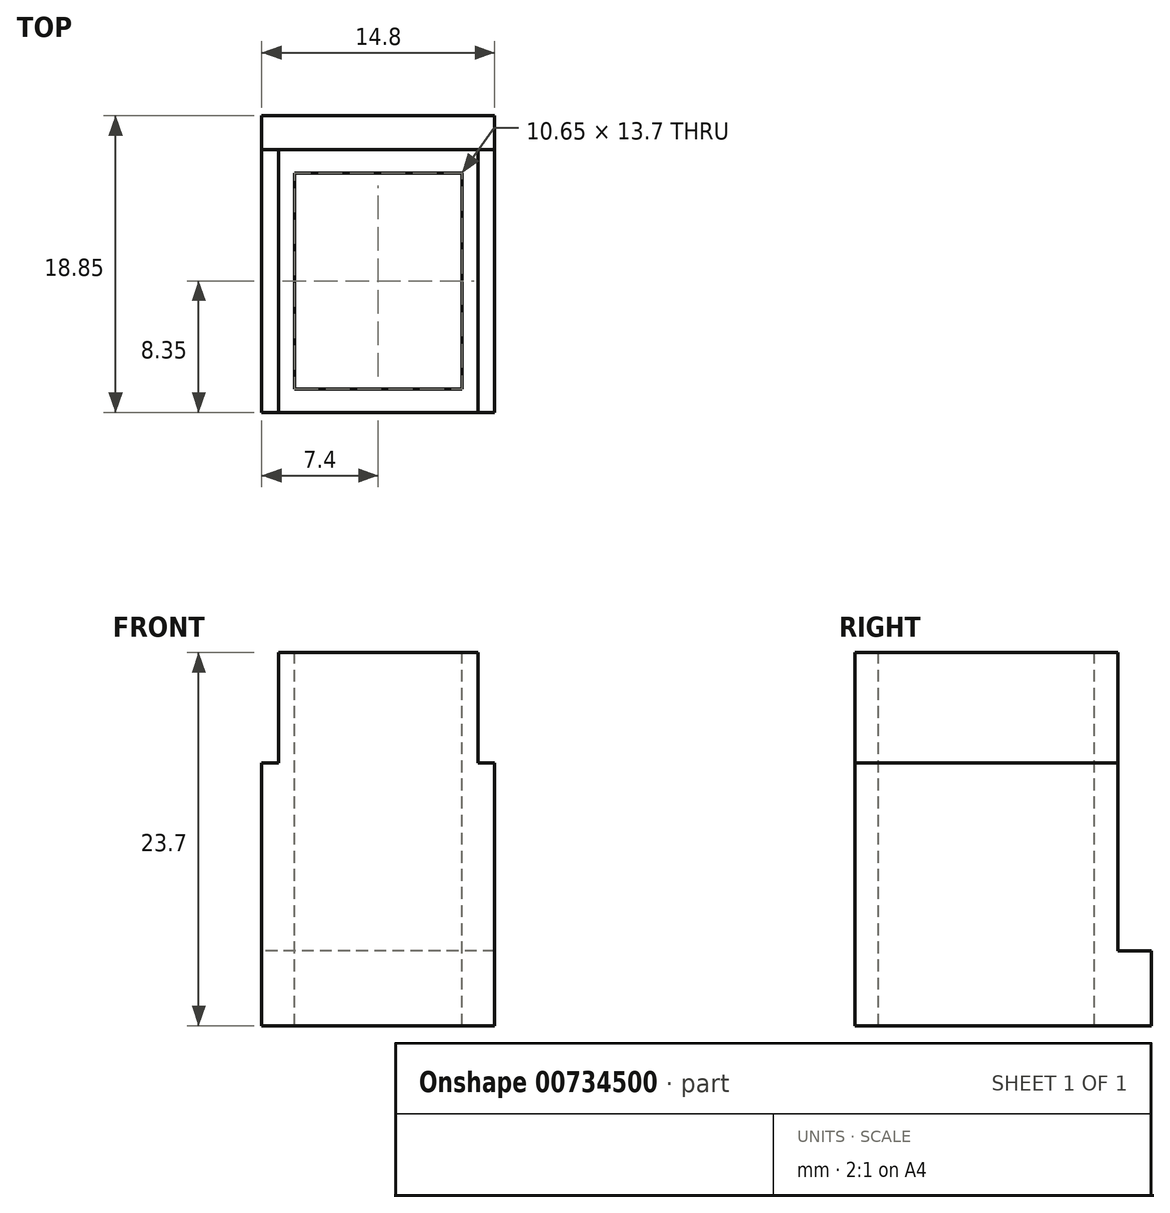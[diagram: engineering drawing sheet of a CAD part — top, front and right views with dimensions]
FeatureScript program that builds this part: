
annotation { "Feature Type Name" : "Feature", "Feature Type Description" : "" }
export const myFeature = defineFeature(function(context is Context, id is Id, definition is map)
    precondition{}
    {
        {
            var Q0;
            Q0=qCreatedBy(makeId("Top.planeOp"),FACE);
            var sketch = newSketch(context, id + "F0", { "sketchPlane" : qUnion([Q0])});
            skLineSegment(sketch, "E0.bottom", {"start": v(5.9, 6.85) * mm, "end": v(-5.9, 6.85) * mm});
            skLineSegment(sketch, "E0.top", {"start": v(5.9, -6.85) * mm, "end": v(-5.9, -6.85) * mm});
            skLineSegment(sketch, "E0.left", {"start": v(5.9, 6.85) * mm, "end": v(5.9, -6.85) * mm});
            skLineSegment(sketch, "E0.right", {"start": v(-5.9, 6.85) * mm, "end": v(-5.9, -6.85) * mm});
            skPoint(sketch, "E0.middle", {"position": v(0, 0) * mm});
            skLineSegment(sketch, "E1.0", {"start": v(-7.4, 8.35) * mm, "end": v(-7.4, -8.35) * mm});
            skLineSegment(sketch, "E1.1", {"start": v(7.4, 8.35) * mm, "end": v(-7.4, 8.35) * mm});
            skLineSegment(sketch, "E1.2", {"start": v(7.4, 8.35) * mm, "end": v(7.4, -8.35) * mm});
            skLineSegment(sketch, "E1.3", {"start": v(7.4, -8.35) * mm, "end": v(-7.4, -8.35) * mm});
            skSolve(sketch);
        }
        {
            var Q0;
            Q0 = qSketchRegion(id + "F0", true);
            extrude(context, id + "F1", {"entities" : qUnion([Q0]), "depth" : 11.95 * mm, "offsetDistance" : 25.4 * mm});
        }
        {
            var Q0;
            Q0=makeQuery(id+"F1.opExtrude","CAP_FACE",FACE,{"disambiguationData":[OSD([sQuery(id+"F0.wireOp",EDGE,"E0.bottom"),sQuery(id+"F0.wireOp",EDGE,"E0.top"),sQuery(id+"F0.wireOp",EDGE,"E0.left"),sQuery(id+"F0.wireOp",EDGE,"E0.right"),sQuery(id+"F0.wireOp",EDGE,"E1.0"),sQuery(id+"F0.wireOp",EDGE,"E1.1"),sQuery(id+"F0.wireOp",EDGE,"E1.2"),sQuery(id+"F0.wireOp",EDGE,"E1.3")])],"isStart":false});
            var sketch = newSketch(context, id + "F2", { "sketchPlane" : qUnion([Q0])});
            skLineSegment(sketch, "E2.bottom", {"start": v(6.32, 8.35) * mm, "end": v(-6.33, 8.35) * mm});
            skLineSegment(sketch, "E2.top", {"start": v(6.33, -8.35) * mm, "end": v(-6.32, -8.35) * mm});
            skLineSegment(sketch, "E2.left", {"start": v(6.32, 8.35) * mm, "end": v(6.33, -8.35) * mm});
            skLineSegment(sketch, "E2.right", {"start": v(-6.33, 8.35) * mm, "end": v(-6.33, -8.35) * mm});
            skPoint(sketch, "E2.middle", {"position": v(0, 0) * mm});
            skLineSegment(sketch, "E3.0", {"start": v(-5.33, 7.35) * mm, "end": v(-5.33, -7.35) * mm});
            skLineSegment(sketch, "E3.1", {"start": v(5.32, 7.35) * mm, "end": v(-5.33, 7.35) * mm});
            skLineSegment(sketch, "E3.2", {"start": v(5.32, 7.35) * mm, "end": v(5.33, -7.35) * mm});
            skLineSegment(sketch, "E3.3", {"start": v(5.33, -7.35) * mm, "end": v(-5.33, -7.35) * mm});
            skSolve(sketch);
        }
        {
            var Q0;
            Q0 = qSketchRegion(id + "F2", true);
            extrude(context, id + "F3", {"entities" : qUnion([Q0]), "operationType" : NewBodyOperationType.ADD, "depth" : 7 * mm, "offsetDistance" : 25.4 * mm});
        }
        {
            var Q0;
            {var subQ1=sQuery(id+"F0.wireOp",EDGE,"E0.right");var subQ3=sQuery(id+"F2.wireOp",EDGE,"E3.0");Q0=makeQuery(id+"F3.boolean.opBoolean","SPLIT",FACE,{"disambiguationData":[TD([makeQuery(id+"F1.opExtrude","SWEPT_FACE",FACE,{"disambiguationData":[OSD([subQ1])]})])],"derivedFrom":makeQuery(id+"F3.opExtrude","CAP_FACE",FACE,{"disambiguationData":[OSD([sQuery(id+"F2.wireOp",EDGE,"E2.bottom"),sQuery(id+"F2.wireOp",EDGE,"E2.top"),sQuery(id+"F2.wireOp",EDGE,"E2.left"),sQuery(id+"F2.wireOp",EDGE,"E2.right"),subQ3,sQuery(id+"F2.wireOp",EDGE,"E3.1"),sQuery(id+"F2.wireOp",EDGE,"E3.2"),sQuery(id+"F2.wireOp",EDGE,"E3.3")])],"isStart":true})});}
            var sketch = newSketch(context, id + "F4", { "sketchPlane" : qUnion([Q0])});
            skLineSegment(sketch, "E4.bottom", {"start": v(-5.9, 6.85) * mm, "end": v(-5.33, 6.85) * mm});
            skLineSegment(sketch, "E4.top", {"start": v(-5.9, -6.85) * mm, "end": v(-5.33, -6.85) * mm});
            skLineSegment(sketch, "E4.left", {"start": v(-5.9, 6.85) * mm, "end": v(-5.9, -6.85) * mm});
            skLineSegment(sketch, "E4.right", {"start": v(-5.33, 6.85) * mm, "end": v(-5.33, -6.85) * mm});
            skSolve(sketch);
        }
        {
            var Q0;
            Q0 = qSketchRegion(id + "F4", true);
            var Q1;
            Q1=makeQuery(id+"F1.opExtrude","CAP_FACE",FACE,{"disambiguationData":[OSD([sQuery(id+"F0.wireOp",EDGE,"E0.bottom"),sQuery(id+"F0.wireOp",EDGE,"E0.top"),sQuery(id+"F0.wireOp",EDGE,"E0.left"),sQuery(id+"F0.wireOp",EDGE,"E0.right"),sQuery(id+"F0.wireOp",EDGE,"E1.0"),sQuery(id+"F0.wireOp",EDGE,"E1.1"),sQuery(id+"F0.wireOp",EDGE,"E1.2"),sQuery(id+"F0.wireOp",EDGE,"E1.3")])],"isStart":true});
            extrude(context, id + "F5", {"entities" : qUnion([Q0]), "operationType" : NewBodyOperationType.ADD, "endBound" : BoundingType.UP_TO_SURFACE, "depth" : 25.4 * mm, "endBoundEntityFace" : qUnion([Q1]), "offsetDistance" : 25.4 * mm});
        }
        {
            var Q0;
            {var subQ0=sQuery(id+"F0.wireOp",EDGE,"E0.left");var subQ3=sQuery(id+"F2.wireOp",EDGE,"E3.2");Q0=makeQuery(id+"F3.boolean.opBoolean","SPLIT",FACE,{"disambiguationData":[TD([makeQuery(id+"F1.opExtrude","SWEPT_FACE",FACE,{"disambiguationData":[OSD([subQ0])]})])],"derivedFrom":makeQuery(id+"F3.opExtrude","CAP_FACE",FACE,{"disambiguationData":[OSD([sQuery(id+"F2.wireOp",EDGE,"E2.bottom"),sQuery(id+"F2.wireOp",EDGE,"E2.top"),sQuery(id+"F2.wireOp",EDGE,"E2.left"),sQuery(id+"F2.wireOp",EDGE,"E2.right"),sQuery(id+"F2.wireOp",EDGE,"E3.0"),sQuery(id+"F2.wireOp",EDGE,"E3.1"),subQ3,sQuery(id+"F2.wireOp",EDGE,"E3.3")])],"isStart":true})});}
            var sketch = newSketch(context, id + "F6", { "sketchPlane" : qUnion([Q0])});
            skLineSegment(sketch, "E5.bottom", {"start": v(5.9, 6.85) * mm, "end": v(5.32, 6.85) * mm});
            skLineSegment(sketch, "E5.top", {"start": v(5.9, -6.85) * mm, "end": v(5.32, -6.85) * mm});
            skLineSegment(sketch, "E5.left", {"start": v(5.9, 6.85) * mm, "end": v(5.9, -6.85) * mm});
            skLineSegment(sketch, "E5.right", {"start": v(5.32, 6.85) * mm, "end": v(5.32, -6.85) * mm});
            skSolve(sketch);
        }
        {
            var Q0;
            Q0 = qSketchRegion(id + "F6", true);
            var Q1;
            {var subQ0=sQuery(id+"F0.wireOp",EDGE,"E1.3");var subQ1=sQuery(id+"F0.wireOp",EDGE,"E1.2");var subQ2=sQuery(id+"F0.wireOp",EDGE,"E1.1");var subQ3=sQuery(id+"F0.wireOp",EDGE,"E1.0");var subQ4=sQuery(id+"F0.wireOp",EDGE,"E0.right");var subQ5=sQuery(id+"F0.wireOp",EDGE,"E0.left");var subQ6=sQuery(id+"F0.wireOp",EDGE,"E0.top");var subQ7=sQuery(id+"F0.wireOp",EDGE,"E0.bottom");Q1=makeQuery(id+"F5.boolean.opBoolean","MERGE",FACE,{"derivedFrom":[makeQuery(id+"F1.opExtrude","CAP_FACE",FACE,{"disambiguationData":[OSD([subQ7,subQ6,subQ5,subQ4,subQ3,subQ2,subQ1,subQ0])],"isStart":true}),makeQuery(id+"F5.opExtrude","CAP_FACE",FACE,{"disambiguationData":[OSD([subQ7,subQ6,subQ5,subQ4,subQ3,subQ2,subQ1,subQ0])],"isStart":false})]});}
            extrude(context, id + "F7", {"entities" : qUnion([Q0]), "operationType" : NewBodyOperationType.ADD, "endBound" : BoundingType.UP_TO_SURFACE, "depth" : 25.4 * mm, "endBoundEntityFace" : qUnion([Q1]), "offsetDistance" : 25.4 * mm});
        }
        {
            var Q0;
            {var subQ3=sQuery(id+"F0.wireOp",EDGE,"E0.bottom");Q0=makeQuery(id+"F3.boolean.opBoolean","SPLIT",FACE,{"disambiguationData":[TD([makeQuery(id+"F1.opExtrude","SWEPT_FACE",FACE,{"disambiguationData":[OSD([subQ3])]})])],"derivedFrom":makeQuery(id+"F1.opExtrude","CAP_FACE",FACE,{"disambiguationData":[OSD([subQ3,sQuery(id+"F0.wireOp",EDGE,"E0.top"),sQuery(id+"F0.wireOp",EDGE,"E0.left"),sQuery(id+"F0.wireOp",EDGE,"E0.right"),sQuery(id+"F0.wireOp",EDGE,"E1.0"),sQuery(id+"F0.wireOp",EDGE,"E1.1"),sQuery(id+"F0.wireOp",EDGE,"E1.2"),sQuery(id+"F0.wireOp",EDGE,"E1.3")])],"isStart":false})});}
            var sketch = newSketch(context, id + "F8", { "sketchPlane" : qUnion([Q0])});
            skLineSegment(sketch, "E6.bottom", {"start": v(-5.33, 7.35) * mm, "end": v(5.32, 7.35) * mm});
            skLineSegment(sketch, "E6.top", {"start": v(-5.33, 6.85) * mm, "end": v(5.32, 6.85) * mm});
            skLineSegment(sketch, "E6.left", {"start": v(-5.33, 7.35) * mm, "end": v(-5.33, 6.85) * mm});
            skLineSegment(sketch, "E6.right", {"start": v(5.32, 7.35) * mm, "end": v(5.32, 6.85) * mm});
            skSolve(sketch);
        }
        {
            var Q0;
            Q0 = qSketchRegion(id + "F8", true);
            var Q1;
            Q1=makeQuery(id+"F3.opExtrude","CAP_FACE",FACE,{"disambiguationData":[OSD([sQuery(id+"F2.wireOp",EDGE,"E2.bottom"),sQuery(id+"F2.wireOp",EDGE,"E2.top"),sQuery(id+"F2.wireOp",EDGE,"E2.left"),sQuery(id+"F2.wireOp",EDGE,"E2.right"),sQuery(id+"F2.wireOp",EDGE,"E3.0"),sQuery(id+"F2.wireOp",EDGE,"E3.1"),sQuery(id+"F2.wireOp",EDGE,"E3.2"),sQuery(id+"F2.wireOp",EDGE,"E3.3")])],"isStart":false});
            extrude(context, id + "F9", {"entities" : qUnion([Q0]), "operationType" : NewBodyOperationType.ADD, "endBound" : BoundingType.UP_TO_SURFACE, "depth" : 25.4 * mm, "endBoundEntityFace" : qUnion([Q1]), "offsetDistance" : 25.4 * mm});
        }
        {
            var Q0;
            {var subQ3=sQuery(id+"F0.wireOp",EDGE,"E0.top");Q0=makeQuery(id+"F3.boolean.opBoolean","SPLIT",FACE,{"disambiguationData":[TD([makeQuery(id+"F1.opExtrude","SWEPT_FACE",FACE,{"disambiguationData":[OSD([subQ3])]})])],"derivedFrom":makeQuery(id+"F1.opExtrude","CAP_FACE",FACE,{"disambiguationData":[OSD([sQuery(id+"F0.wireOp",EDGE,"E0.bottom"),subQ3,sQuery(id+"F0.wireOp",EDGE,"E0.left"),sQuery(id+"F0.wireOp",EDGE,"E0.right"),sQuery(id+"F0.wireOp",EDGE,"E1.0"),sQuery(id+"F0.wireOp",EDGE,"E1.1"),sQuery(id+"F0.wireOp",EDGE,"E1.2"),sQuery(id+"F0.wireOp",EDGE,"E1.3")])],"isStart":false})});}
            var sketch = newSketch(context, id + "F10", { "sketchPlane" : qUnion([Q0])});
            skLineSegment(sketch, "E7.bottom", {"start": v(-5.33, -6.85) * mm, "end": v(5.33, -6.85) * mm});
            skLineSegment(sketch, "E7.top", {"start": v(-5.33, -7.35) * mm, "end": v(5.33, -7.35) * mm});
            skLineSegment(sketch, "E7.left", {"start": v(-5.33, -6.85) * mm, "end": v(-5.33, -7.35) * mm});
            skLineSegment(sketch, "E7.right", {"start": v(5.33, -6.85) * mm, "end": v(5.33, -7.35) * mm});
            skSolve(sketch);
        }
        {
            var Q0;
            Q0 = qSketchRegion(id + "F10", true);
            var Q1;
            {var subQ0=sQuery(id+"F2.wireOp",EDGE,"E3.3");var subQ1=sQuery(id+"F2.wireOp",EDGE,"E3.2");var subQ2=sQuery(id+"F2.wireOp",EDGE,"E3.1");var subQ3=sQuery(id+"F2.wireOp",EDGE,"E3.0");var subQ4=sQuery(id+"F2.wireOp",EDGE,"E2.right");var subQ5=sQuery(id+"F2.wireOp",EDGE,"E2.left");var subQ6=sQuery(id+"F2.wireOp",EDGE,"E2.top");var subQ7=sQuery(id+"F2.wireOp",EDGE,"E2.bottom");Q1=makeQuery(id+"F9.boolean.opBoolean","MERGE",FACE,{"derivedFrom":[makeQuery(id+"F3.opExtrude","CAP_FACE",FACE,{"disambiguationData":[OSD([subQ7,subQ6,subQ5,subQ4,subQ3,subQ2,subQ1,subQ0])],"isStart":false}),makeQuery(id+"F9.opExtrude","CAP_FACE",FACE,{"disambiguationData":[OSD([subQ7,subQ6,subQ5,subQ4,subQ3,subQ2,subQ1,subQ0])],"isStart":false})]});}
            extrude(context, id + "F11", {"entities" : qUnion([Q0]), "operationType" : NewBodyOperationType.ADD, "endBound" : BoundingType.UP_TO_SURFACE, "depth" : 25.4 * mm, "endBoundEntityFace" : qUnion([Q1]), "offsetDistance" : 25.4 * mm});
        }
        {
            var Q0;
            {var subQ0=sQuery(id+"F0.wireOp",EDGE,"E1.3");var subQ1=sQuery(id+"F0.wireOp",EDGE,"E1.2");var subQ2=sQuery(id+"F0.wireOp",EDGE,"E1.1");var subQ3=sQuery(id+"F0.wireOp",EDGE,"E1.0");var subQ4=sQuery(id+"F0.wireOp",EDGE,"E0.right");var subQ5=sQuery(id+"F0.wireOp",EDGE,"E0.left");var subQ6=sQuery(id+"F0.wireOp",EDGE,"E0.top");var subQ7=sQuery(id+"F0.wireOp",EDGE,"E0.bottom");Q0=makeQuery(id+"F7.boolean.opBoolean","MERGE",FACE,{"derivedFrom":[makeQuery(id+"F5.boolean.opBoolean","MERGE",FACE,{"derivedFrom":[makeQuery(id+"F1.opExtrude","CAP_FACE",FACE,{"disambiguationData":[OSD([subQ7,subQ6,subQ5,subQ4,subQ3,subQ2,subQ1,subQ0])],"isStart":true}),makeQuery(id+"F5.opExtrude","CAP_FACE",FACE,{"disambiguationData":[OSD([subQ7,subQ6,subQ5,subQ4,subQ3,subQ2,subQ1,subQ0])],"isStart":false})]}),makeQuery(id+"F7.opExtrude","CAP_FACE",FACE,{"disambiguationData":[OSD([subQ7,subQ6,subQ5,subQ4,subQ3,subQ2,subQ1,subQ0])],"isStart":false})]});}
            var sketch = newSketch(context, id + "F12", { "sketchPlane" : qUnion([Q0])});
            skLineSegment(sketch, "E8.bottom", {"start": v(-7.4, 8.35) * mm, "end": v(7.4, 8.35) * mm});
            skLineSegment(sketch, "E8.top", {"start": v(-7.4, -10.5) * mm, "end": v(7.4, -10.5) * mm});
            skLineSegment(sketch, "E8.left", {"start": v(-7.4, 8.35) * mm, "end": v(-7.4, -10.5) * mm});
            skLineSegment(sketch, "E8.right", {"start": v(7.4, 8.35) * mm, "end": v(7.4, -10.5) * mm});
            skLineSegment(sketch, "E9.bottom", {"start": v(-5.33, 6.85) * mm, "end": v(5.33, 6.85) * mm});
            skLineSegment(sketch, "E9.top", {"start": v(-5.33, -6.85) * mm, "end": v(5.33, -6.85) * mm});
            skLineSegment(sketch, "E9.left", {"start": v(-5.33, 6.85) * mm, "end": v(-5.33, -6.85) * mm});
            skLineSegment(sketch, "E9.right", {"start": v(5.33, 6.85) * mm, "end": v(5.33, -6.85) * mm});
            skSolve(sketch);
        }
        {
            var Q0;
            Q0 = qSketchRegion(id + "F12", true);
            extrude(context, id + "F13", {"entities" : qUnion([Q0]), "operationType" : NewBodyOperationType.ADD, "depth" : 4.75 * mm, "offsetDistance" : 25.4 * mm});
        }
    });
